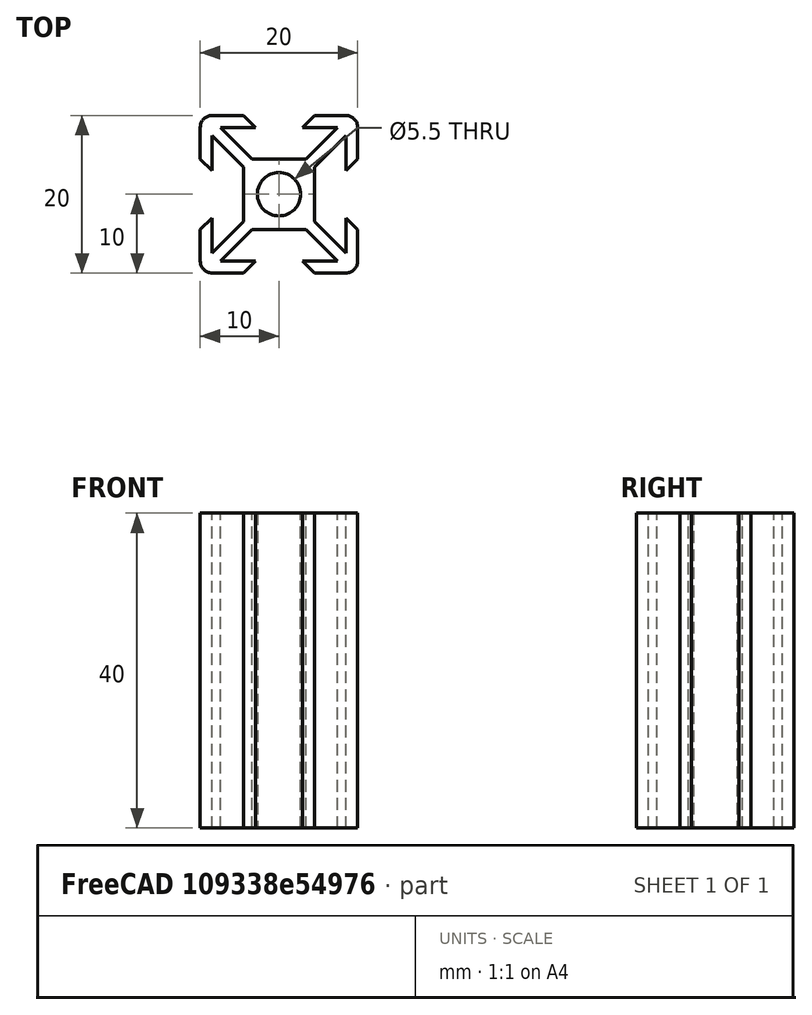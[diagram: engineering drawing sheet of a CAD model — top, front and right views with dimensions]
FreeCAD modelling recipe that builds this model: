
FCSTD DOCUMENT  (FreeCAD 0.20R29603 (Git))
Label: normal_2020_beam_40mm
License: All rights reserved
LicenseURL: http://en.wikipedia.org/wiki/All_rights_reserved
objects: Spreadsheet::Sheet×1, Sketcher::SketchObject×1, PartDesign::Pad×1, PartDesign::Body×1
note: 4 computed .brp shape members not serialized (recipe doc carries the construction recipe); baked Part::Feature solids carry a one-line shape summary decoded from their .brp

FEATURE [Spreadsheet::Sheet] Spreadsheet  label="parameters"
  cells = A1=Beam dimensions; A2=Length; B2(beam_length)=40
FEATURE [Sketcher::SketchObject] Sketch
  FullyConstrained = true
  MapMode = 5
  Support = -> [XY_Plane]
  sketch-geometry (57):
    g0: Circle CenterX=0 CenterY=0 CenterZ=0 NormalX=0 NormalY=0 NormalZ=1 AngleXU=0 Radius=2.75
    g1: LineSegment StartX=-4.5 StartY=4.5 StartZ=0 EndX=4.5 EndY=4.5 EndZ=0
    g2: LineSegment StartX=4.5 StartY=4.5 StartZ=0 EndX=4.5 EndY=-4.5 EndZ=0
    g3: LineSegment StartX=4.5 StartY=-4.5 StartZ=0 EndX=-4.5 EndY=-4.5 EndZ=0
    g4: LineSegment StartX=-4.5 StartY=-4.5 StartZ=0 EndX=-4.5 EndY=4.5 EndZ=0
    g5: LineSegment StartX=-10 StartY=10 StartZ=0 EndX=10 EndY=10 EndZ=0
    g6: LineSegment StartX=10 StartY=10 StartZ=0 EndX=10 EndY=-10 EndZ=0
    g7: LineSegment StartX=10 StartY=-10 StartZ=0 EndX=-10 EndY=-10 EndZ=0
    g8: LineSegment StartX=-10 StartY=-10 StartZ=0 EndX=-10 EndY=10 EndZ=0
    g9: LineSegment StartX=-8.5 StartY=8.5 StartZ=0 EndX=8.5 EndY=8.5 EndZ=0
    g10: LineSegment StartX=8.5 StartY=8.5 StartZ=0 EndX=8.5 EndY=-8.5 EndZ=0
    g11: LineSegment StartX=8.5 StartY=-8.5 StartZ=0 EndX=-8.5 EndY=-8.5 EndZ=0
    g12: LineSegment StartX=-8.5 StartY=-8.5 StartZ=0 EndX=-8.5 EndY=8.5 EndZ=0
    g13: ArcOfCircle CenterX=-8.5 CenterY=8.5 CenterZ=0 NormalX=0 NormalY=0 NormalZ=1 AngleXU=0 Radius=1.5 StartAngle=1.5708 EndAngle=3.14159
    g14: ArcOfCircle CenterX=8.5 CenterY=8.5 CenterZ=0 NormalX=0 NormalY=0 NormalZ=1 AngleXU=0 Radius=1.5 StartAngle=2.20881e-08 EndAngle=1.5708
    g15: ArcOfCircle CenterX=8.5 CenterY=-8.5 CenterZ=0 NormalX=0 NormalY=0 NormalZ=1 AngleXU=0 Radius=1.5 StartAngle=4.71239 EndAngle=6.28319
    g16: ArcOfCircle CenterX=-8.5 CenterY=-8.5 CenterZ=0 NormalX=0 NormalY=0 NormalZ=1 AngleXU=0 Radius=1.5 StartAngle=3.14159 EndAngle=4.71239
    g17: LineSegment StartX=7.43934 StartY=8.5 StartZ=0 EndX=8.5 EndY=7.43934 EndZ=0
    g18: LineSegment StartX=8.5 StartY=10 StartZ=0 EndX=4.5 EndY=10 EndZ=0
    g19: LineSegment StartX=4.5 StartY=10 StartZ=0 EndX=3 EndY=8.5 EndZ=0
    g20: LineSegment StartX=3 StartY=8.5 StartZ=0 EndX=7.43934 EndY=8.5 EndZ=0
    g21: LineSegment StartX=7.43934 StartY=8.5 StartZ=0 EndX=3.43934 EndY=4.5 EndZ=0
    g22: LineSegment StartX=-8.5 StartY=10 StartZ=0 EndX=-4.5 EndY=10 EndZ=0
    g23: LineSegment StartX=-4.5 StartY=10 StartZ=0 EndX=-3 EndY=8.5 EndZ=0
    g24: LineSegment StartX=-7.43934 StartY=8.5 StartZ=0 EndX=-8.5 EndY=7.43934 EndZ=0
    g25: LineSegment StartX=-8.5 StartY=-7.43934 StartZ=0 EndX=-7.43934 EndY=-8.5 EndZ=0
    g26: LineSegment StartX=8.5 StartY=-7.43934 StartZ=0 EndX=7.43934 EndY=-8.5 EndZ=0
    g27: LineSegment StartX=-3 StartY=8.5 StartZ=0 EndX=-7.43934 EndY=8.5 EndZ=0
    g28: LineSegment StartX=-7.43934 StartY=8.5 StartZ=0 EndX=-3.43934 EndY=4.5 EndZ=0
    g29: LineSegment StartX=-3.43934 StartY=4.5 StartZ=0 EndX=3.43934 EndY=4.5 EndZ=0
    g30: LineSegment StartX=-10 StartY=8.5 StartZ=0 EndX=-10 EndY=4.5 EndZ=0
    g31: LineSegment StartX=-10 StartY=4.5 StartZ=0 EndX=-8.5 EndY=3 EndZ=0
    g32: LineSegment StartX=-8.5 StartY=3 StartZ=0 EndX=-8.5 EndY=7.43934 EndZ=0
    g33: LineSegment StartX=-8.5 StartY=7.43934 StartZ=0 EndX=-4.5 EndY=3.43934 EndZ=0
    g34: LineSegment StartX=-4.5 StartY=3.43934 StartZ=0 EndX=-4.5 EndY=-3.43934 EndZ=0
    g35: LineSegment StartX=-4.5 StartY=-3.43934 StartZ=0 EndX=-8.5 EndY=-7.43934 EndZ=0
    g36: LineSegment StartX=-8.5 StartY=-7.43934 StartZ=0 EndX=-8.5 EndY=-3 EndZ=0
    g37: LineSegment StartX=-8.5 StartY=-3 StartZ=0 EndX=-10 EndY=-4.5 EndZ=0
    g38: LineSegment StartX=-10 StartY=-4.5 StartZ=0 EndX=-10 EndY=-8.5 EndZ=0
    g39: LineSegment StartX=-8.5 StartY=-10 StartZ=0 EndX=-4.5 EndY=-10 EndZ=0
    g40: LineSegment StartX=-4.5 StartY=-10 StartZ=0 EndX=-3 EndY=-8.5 EndZ=0
    g41: LineSegment StartX=-3 StartY=-8.5 StartZ=0 EndX=-7.43934 EndY=-8.5 EndZ=0
    g42: LineSegment StartX=-7.43934 StartY=-8.5 StartZ=0 EndX=-3.43934 EndY=-4.5 EndZ=0
    g43: LineSegment StartX=-3.43934 StartY=-4.5 StartZ=0 EndX=3.43934 EndY=-4.5 EndZ=0
    g44: LineSegment StartX=3.43934 StartY=-4.5 StartZ=0 EndX=7.43934 EndY=-8.5 EndZ=0
    g45: LineSegment StartX=7.43934 StartY=-8.5 StartZ=0 EndX=3 EndY=-8.5 EndZ=0
    g46: LineSegment StartX=3 StartY=-8.5 StartZ=0 EndX=4.5 EndY=-10 EndZ=0
    g47: LineSegment StartX=4.5 StartY=-10 StartZ=0 EndX=8.5 EndY=-10 EndZ=0
    g48: LineSegment StartX=10 StartY=-8.5 StartZ=0 EndX=10 EndY=-4.5 EndZ=0
    g49: LineSegment StartX=10 StartY=-4.5 StartZ=0 EndX=8.5 EndY=-3 EndZ=0
    g50: LineSegment StartX=8.5 StartY=-3 StartZ=0 EndX=8.5 EndY=-7.43934 EndZ=0
    g51: LineSegment StartX=8.5 StartY=-7.43934 StartZ=0 EndX=4.5 EndY=-3.43934 EndZ=0
    g52: LineSegment StartX=4.5 StartY=-3.43934 StartZ=0 EndX=4.5 EndY=3.43934 EndZ=0
    g53: LineSegment StartX=4.5 StartY=3.43934 StartZ=0 EndX=8.5 EndY=7.43934 EndZ=0
    g54: LineSegment StartX=8.5 StartY=7.43934 StartZ=0 EndX=8.5 EndY=3 EndZ=0
    g55: LineSegment StartX=8.5 StartY=3 StartZ=0 EndX=10 EndY=4.5 EndZ=0
    g56: LineSegment StartX=10 StartY=4.5 StartZ=0 EndX=10 EndY=8.5 EndZ=0
  constraints (158):
    c: Coincident(g0,g-1)
    c: Coincident(g1,g2)
    c: Coincident(g2,g3)
    c: Coincident(g3,g4)
    c: Coincident(g4,g1)
    c: Horizontal(g1)
    c: Horizontal(g3)
    c: Vertical(g2)
    c: Vertical(g4)
    c: Symmetric(g1,g3,g0)
    c: Diameter(g0) = 5.5
    c: Equal(g1,g2)
    c: Distance(g1) = 9
    c: Coincident(g5,g6)
    c: Coincident(g6,g7)
    c: Coincident(g7,g8)
    c: Coincident(g8,g5)
    c: Horizontal(g5)
    c: Horizontal(g7)
    c: Vertical(g6)
    c: Vertical(g8)
    c: Symmetric(g5,g7,g0)
    c: Distance(g5) = 20
    c: Equal(g5,g6)
    c: Coincident(g9,g10)
    c: Coincident(g10,g11)
    c: Coincident(g11,g12)
    c: Coincident(g12,g9)
    c: Horizontal(g9)
    c: Horizontal(g11)
    c: Vertical(g10)
    c: Vertical(g12)
    c: Symmetric(g9,g11,g0)
    c: Distance(g9) = 17
    c: Equal(g9,g10)
    c: Coincident(g13,g9)
    c: PointOnObject(g13,g5)
    c: PointOnObject(g13,g8)
    c: Vertical(g13,g13)
    c: Coincident(g14,g9)
    c: PointOnObject(g14,g5)
    c: PointOnObject(g14,g6)
    c: Vertical(g14,g14)
    c: Coincident(g15,g10)
    c: PointOnObject(g15,g6)
    c: PointOnObject(g15,g7)
    c: Vertical(g15,g15)
    c: Coincident(g16,g11)
    c: PointOnObject(g16,g7)
    c: PointOnObject(g16,g8)
    c: Vertical(g16,g16)
    c: PointOnObject(g17,g9)
    c: PointOnObject(g17,g10)
    c: Distance(g17) = 1.5
    c: Angle(g17,g10) = 2.35619
    c: Tangent(g14,g18) = -1.5708
    c: Coincident(g18,g19)
    c: PointOnObject(g19,g9)
    c: Coincident(g19,g20)
    c: Coincident(g20,g17)
    c: Coincident(g20,g21)
    c: PointOnObject(g21,g1)
    c: Angle(g19,g18) = 2.35619
    c: Tangent(g13,g22) = 1.5708
    c: Coincident(g22,g23)
    c: PointOnObject(g23,g9)
    c: PointOnObject(g24,g9)
    c: PointOnObject(g24,g12)
    c: PointOnObject(g25,g12)
    c: PointOnObject(g25,g11)
    c: PointOnObject(g26,g10)
    c: PointOnObject(g26,g11)
    c: Equal(g24,g17)
    c: Equal(g17,g25)
    c: Equal(g17,g26)
    c: Horizontal(g24,g17)
    c: Vertical(g20,g26)
    c: Horizontal(g26,g25)
    c: Coincident(g23,g27)
    c: Coincident(g27,g24)
    c: Coincident(g27,g28)
    c: PointOnObject(g28,g1)
    c: Distance(g19,g23) = 6
    c: Angle(g22,g23) = 2.35619
    c: Equal(g27,g20)
    c: Angle(g20,g21) = 0.785398
    c: Equal(g21,g28)
    c: Coincident(g29,g28)
    c: Coincident(g29,g21)
    c: Tangent(g13,g30) = -1.5708
    c: Coincident(g30,g31)
    c: PointOnObject(g31,g12)
    c: Coincident(g31,g32)
    c: Coincident(g32,g24)
    c: Coincident(g32,g33)
    c: PointOnObject(g33,g4)
    c: Coincident(g33,g34)
    c: PointOnObject(g34,g4)
    c: Coincident(g34,g35)
    c: Coincident(g35,g25)
    c: Coincident(g35,g36)
    c: PointOnObject(g36,g12)
    c: Coincident(g36,g37)
    c: PointOnObject(g37,g8)
    c: Coincident(g37,g38)
    c: Coincident(g38,g16)
    c: Tangent(g16,g39) = -1.5708
    c: Coincident(g39,g40)
    c: PointOnObject(g40,g11)
    c: Coincident(g40,g41)
    c: Coincident(g41,g25)
    c: Coincident(g41,g42)
    c: PointOnObject(g42,g3)
    c: Coincident(g42,g43)
    c: PointOnObject(g43,g3)
    c: Coincident(g43,g44)
    c: Coincident(g44,g26)
    c: Coincident(g44,g45)
    c: PointOnObject(g45,g11)
    c: Coincident(g45,g46)
    c: PointOnObject(g46,g7)
    c: Coincident(g46,g47)
    c: Coincident(g47,g15)
    c: Tangent(g15,g48) = -1.5708
    c: Coincident(g48,g49)
    c: PointOnObject(g49,g10)
    c: Coincident(g49,g50)
    c: Coincident(g50,g26)
    c: Coincident(g50,g51)
    c: PointOnObject(g51,g2)
    c: Coincident(g51,g52)
    c: PointOnObject(g52,g2)
    c: Coincident(g52,g53)
    c: Coincident(g53,g17)
    c: Coincident(g53,g54)
    c: PointOnObject(g54,g10)
    c: Coincident(g54,g55)
    c: PointOnObject(g55,g6)
    c: Coincident(g55,g56)
    c: Coincident(g56,g14)
    c: Equal(g21,g53)
    c: Equal(g21,g51)
    c: Equal(g21,g44)
    c: Equal(g21,g42)
    c: Equal(g21,g35)
    c: Equal(g20,g32)
    c: Equal(g20,g36)
    c: Equal(g20,g41)
    c: Vertical(g22,g39)
    c: Vertical(g18,g46)
    c: Equal(g20,g45)
    c: Equal(g21,g33)
    c: Angle(g31,g30) = 2.35619
    c: Angle(g38,g37) = 2.35619
    c: Horizontal(g31,g54)
    c: Horizontal(g30,g55)
    c: Horizontal(g36,g49)
    c: Horizontal(g37,g48)
FEATURE [PartDesign::Pad] Pad  label="extrusion_body"
  Direction = (0,0,1)
  Length = 40
  Length2 = 10
  Profile = -> Sketch
  ReferenceAxis = -> Sketch [N_Axis]
  Type = 0
  expr: Length = <<parameters>>.beam_length
FEATURE [PartDesign::Body] Body  label="normal_2020_beam"
  Group = -> [Sketch,Pad]
  Origin = -> Origin
  Tip = -> Pad
